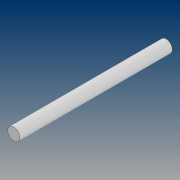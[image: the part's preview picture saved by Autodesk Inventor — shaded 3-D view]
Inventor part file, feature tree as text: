
AUTODESK INVENTOR PART (.ipt)
format: ipt  version: 2021 (Build 250183000, 183)  size: 73,728 bytes
history: native  units: mm
features: extrude x1, sketch x1
ambient origin geometry x8: Origin, YZ Plane, XZ Plane, XY Plane, X Axis, Y Axis, Z Axis, Center Point
bodies: Solid1 (feature_tree)
feature tree (2):
  extrude  "Extrusion1"  Depth=100.0mm TaperAngle=0.0deg
  sketch  "Sketch1"  dims[d0=8.0mm d1=100.0mm d2=0.0mm]
